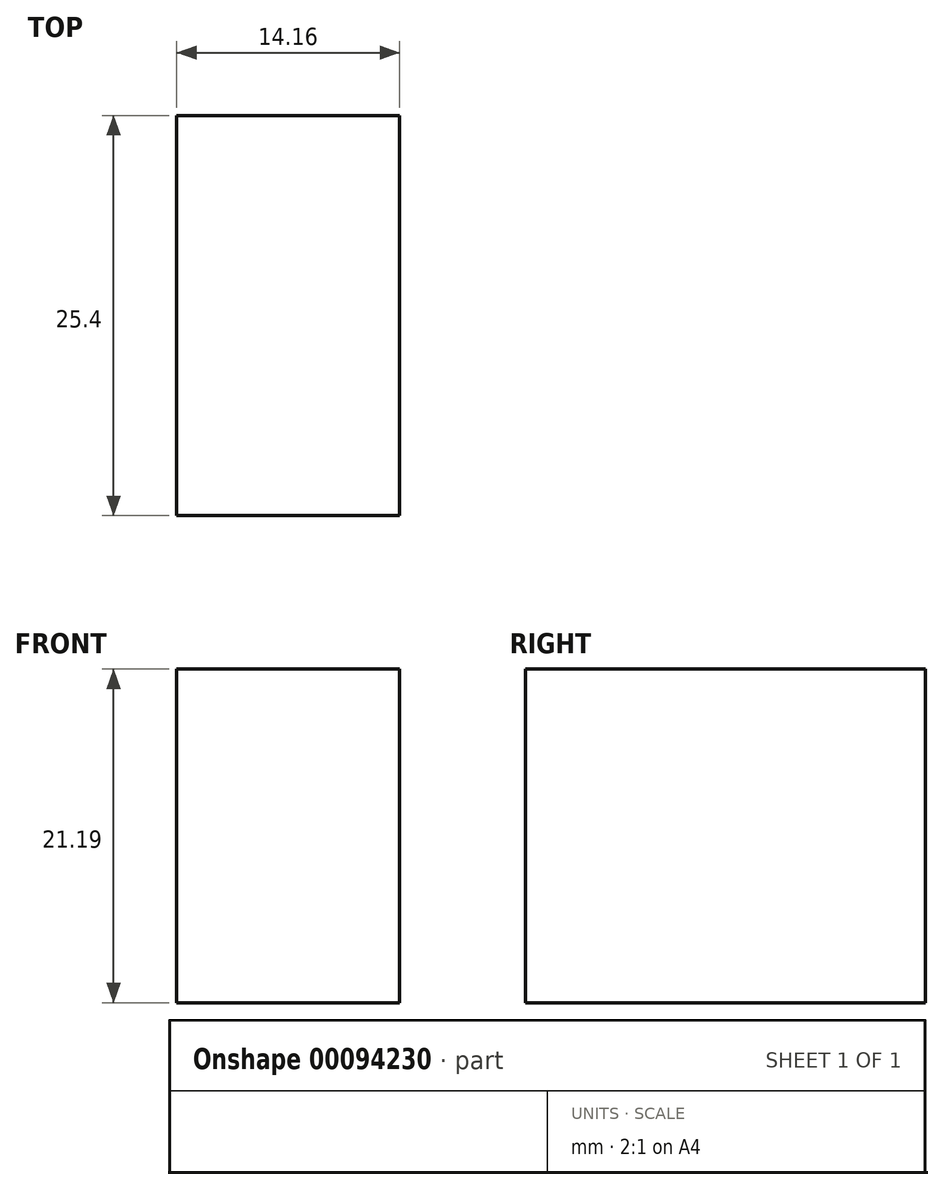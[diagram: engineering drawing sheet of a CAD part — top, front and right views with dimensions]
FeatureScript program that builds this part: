
annotation { "Feature Type Name" : "Feature", "Feature Type Description" : "" }
export const myFeature = defineFeature(function(context is Context, id is Id, definition is map)
    precondition{}
    {
        {
            var Q0;
            Q0=qCreatedBy(makeId("Front.planeOp"),FACE);
            var sketch = newSketch(context, id + "F0", { "sketchPlane" : qUnion([Q0])});
            skLineSegment(sketch, "E0.bottom", {"start": v(-65.4, 44) * mm, "end": v(-51.24, 44) * mm});
            skLineSegment(sketch, "E0.top", {"start": v(-65.4, 22.8) * mm, "end": v(-51.24, 22.8) * mm});
            skLineSegment(sketch, "E0.left", {"start": v(-65.4, 44) * mm, "end": v(-65.4, 22.8) * mm});
            skLineSegment(sketch, "E0.right", {"start": v(-51.24, 44) * mm, "end": v(-51.24, 22.8) * mm});
            skSolve(sketch);
        }
        {
            var Q0;
            Q0=makeQuery(id+"F0.imprint","IMPRINT",FACE,{"disambiguationData":[TD([[makeQuery(id+"F0.imprint","IMPRINT",EDGE,{"derivedFrom":sQuery(id+"F0.wireOp",EDGE,"E0.bottom")}),-1.0]])]});
            extrude(context, id + "F1", {"entities" : qUnion([Q0]), "depth" : 25.4 * mm});
        }
    });
